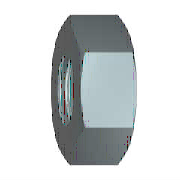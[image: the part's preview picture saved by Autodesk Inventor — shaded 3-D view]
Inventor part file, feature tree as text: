
AUTODESK INVENTOR PART (.ipt)
format: ipt  version: 2022 (Build 260153000, 153)  size: 175,616 bytes
history: native  units: mm (DEFAULTED — no unit token found)
features: sketch x3, other x2, extrude x1, hole x1, plane x1
ambient origin geometry x7: Origin, YZ Plane, XZ Plane, X Axis, Y Axis, Z Axis, Center Point
bodies: Solid1 (feature_tree)
feature tree (8):
  extrude  "Базовый элемент"  Depth=8.082904mm
  other  "Фаска1"
  hole  "Резьба"  [1 undecoded]
  other  "Work Axis1"
  plane  "Work Plane1"
  sketch  "Эскиз1"
  sketch  "Эскиз2"
  sketch  "Эскиз3"
note: 1 required parameter value undecoded (feature->parameter linkage not recoverable at this tier; creation-order binding heuristic only, values carry confidence <= 0.55)
